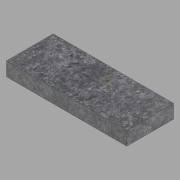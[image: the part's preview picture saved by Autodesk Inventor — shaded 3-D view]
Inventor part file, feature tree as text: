
AUTODESK INVENTOR PART (.ipt)
format: ipt  version: 2022.1 (Build 261234020, 234B)  size: 107,008 bytes
history: native  units: in
note: dims shown in document units (in); Inventor stores cm internally (conversion verified against a paired STEP export)
features: extrude x1, sketch x1
ambient origin geometry x8: Origin, YZ Plane, XZ Plane, XY Plane, X Axis, Y Axis, Z Axis, Center Point
bodies: Solid1 (feature_tree)
feature tree (2):
  extrude  "Extrusion1"  Depth=7.625in
  sketch  "Sketch1"  dims[d0=2.25in d1=7.625in d2=19.625in d3=0.0in]
